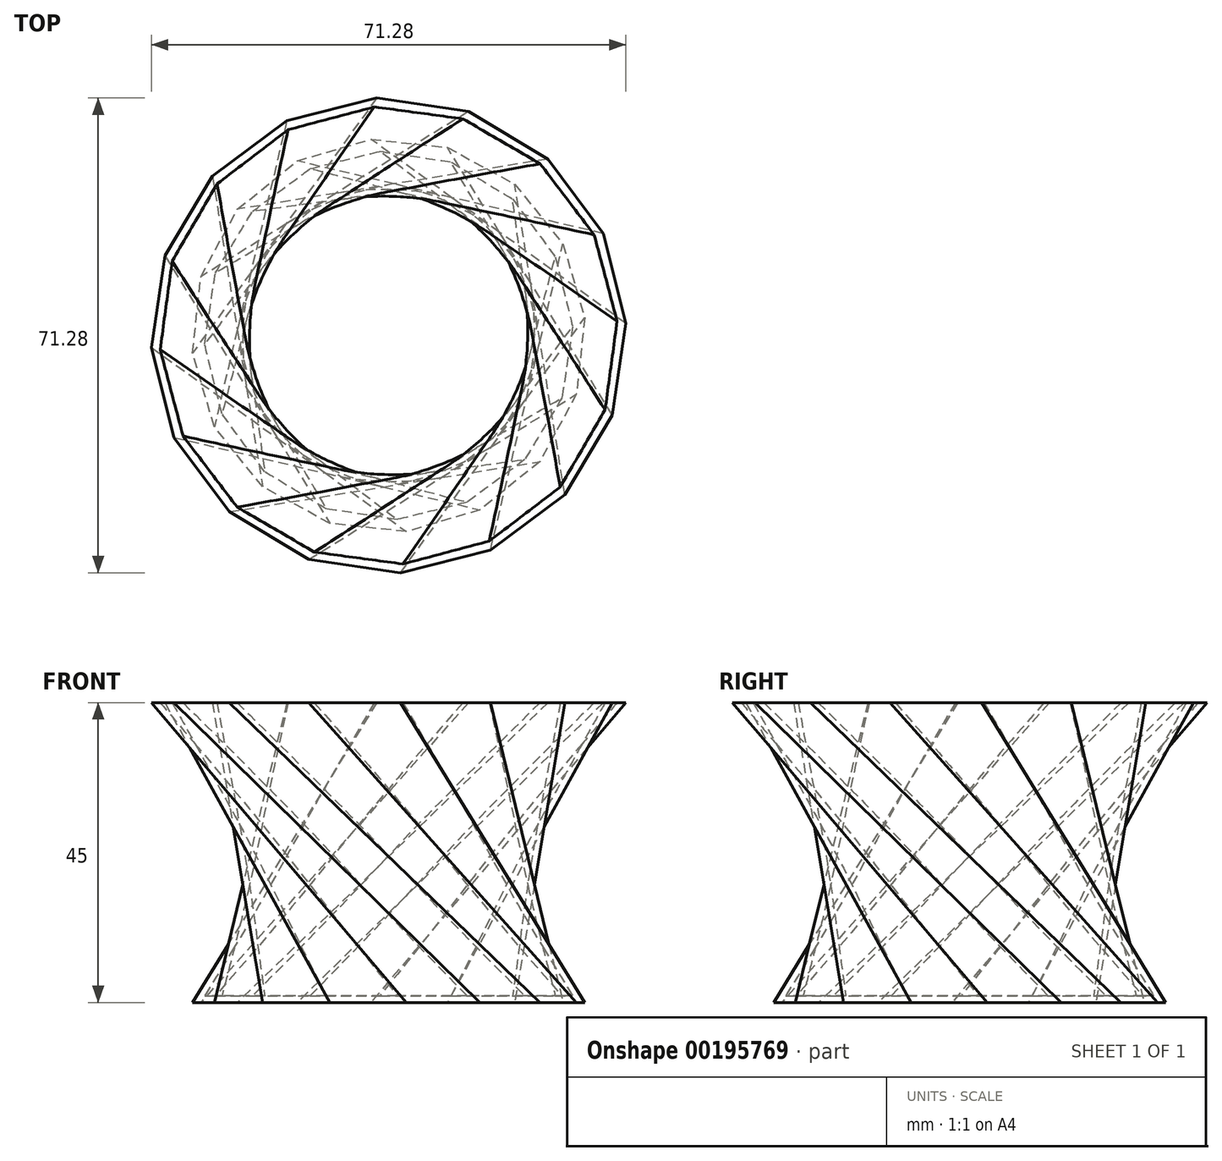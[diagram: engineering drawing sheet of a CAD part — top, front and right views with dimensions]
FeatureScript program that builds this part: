
annotation { "Feature Type Name" : "Feature", "Feature Type Description" : "" }
export const myFeature = defineFeature(function(context is Context, id is Id, definition is map)
    precondition{}
    {
        {
            var Q0;
            Q0=qCreatedBy(makeId("Top.planeOp"),FACE);
            var sketch = newSketch(context, id + "F0", { "sketchPlane" : qUnion([Q0])});
            skCircle(sketch, "E0.cCircle", {"center": v(0, 0) * mm, "radius": 29 * mm, "construction": true});
            skLineSegment(sketch, "E0.0", {"start": v(22.7, -18.94) * mm, "end": v(13.73, -26.19) * mm});
            skLineSegment(sketch, "E0.1", {"start": v(13.73, -26.19) * mm, "end": v(2.66, -29.45) * mm});
            skLineSegment(sketch, "E0.2", {"start": v(2.66, -29.45) * mm, "end": v(-8.81, -28.22) * mm});
            skLineSegment(sketch, "E0.3", {"start": v(-8.81, -28.22) * mm, "end": v(-18.94, -22.7) * mm});
            skLineSegment(sketch, "E0.4", {"start": v(-18.94, -22.7) * mm, "end": v(-26.19, -13.73) * mm});
            skLineSegment(sketch, "E0.5", {"start": v(-26.19, -13.73) * mm, "end": v(-29.45, -2.66) * mm});
            skLineSegment(sketch, "E0.6", {"start": v(-29.45, -2.66) * mm, "end": v(-28.22, 8.81) * mm});
            skLineSegment(sketch, "E0.7", {"start": v(-28.22, 8.81) * mm, "end": v(-22.7, 18.94) * mm});
            skLineSegment(sketch, "E0.8", {"start": v(-22.7, 18.94) * mm, "end": v(-13.73, 26.19) * mm});
            skLineSegment(sketch, "E0.9", {"start": v(-13.73, 26.19) * mm, "end": v(-2.66, 29.45) * mm});
            skLineSegment(sketch, "E0.10", {"start": v(-2.66, 29.45) * mm, "end": v(8.81, 28.22) * mm});
            skLineSegment(sketch, "E0.11", {"start": v(8.81, 28.22) * mm, "end": v(18.94, 22.7) * mm});
            skLineSegment(sketch, "E0.12", {"start": v(18.94, 22.7) * mm, "end": v(26.19, 13.73) * mm});
            skLineSegment(sketch, "E0.13", {"start": v(26.19, 13.73) * mm, "end": v(29.45, 2.66) * mm});
            skLineSegment(sketch, "E0.14", {"start": v(29.45, 2.66) * mm, "end": v(28.22, -8.81) * mm});
            skLineSegment(sketch, "E0.15", {"start": v(28.22, -8.81) * mm, "end": v(22.7, -18.94) * mm});
            skPoint(sketch, "E0.0.midPoint", {"position": v(18.21, -22.57) * mm});
            skSolve(sketch);
        }
        {
            var Q0;
            Q0=qCreatedBy(makeId("Top.planeOp"),FACE);
            cPlane(context, id + "F1", {"entities" : qUnion([Q0]), "cplaneType" : CPlaneType.OFFSET, "offset" : 45 * mm, "width" : 150 * mm, "height" : 150 * mm});
        }
        {
            var Q0;
            Q0=qCreatedBy(id+"F1.planeOp",FACE);
            var sketch = newSketch(context, id + "F2", { "sketchPlane" : qUnion([Q0])});
            skCircle(sketch, "E1.cCircle", {"center": v(0, 0) * mm, "radius": 35 * mm, "construction": true});
            skLineSegment(sketch, "E1.0", {"start": v(-23.93, -26.47) * mm, "end": v(-32.24, -15.3) * mm});
            skLineSegment(sketch, "E1.1", {"start": v(-32.24, -15.3) * mm, "end": v(-35.64, -1.8) * mm});
            skLineSegment(sketch, "E1.2", {"start": v(-35.64, -1.8) * mm, "end": v(-33.61, 11.98) * mm});
            skLineSegment(sketch, "E1.3", {"start": v(-33.61, 11.98) * mm, "end": v(-26.47, 23.93) * mm});
            skLineSegment(sketch, "E1.4", {"start": v(-26.47, 23.93) * mm, "end": v(-15.3, 32.24) * mm});
            skLineSegment(sketch, "E1.5", {"start": v(-15.3, 32.24) * mm, "end": v(-1.8, 35.64) * mm});
            skLineSegment(sketch, "E1.6", {"start": v(-1.8, 35.64) * mm, "end": v(11.98, 33.61) * mm});
            skLineSegment(sketch, "E1.7", {"start": v(11.98, 33.61) * mm, "end": v(23.93, 26.47) * mm});
            skLineSegment(sketch, "E1.8", {"start": v(23.93, 26.47) * mm, "end": v(32.24, 15.3) * mm});
            skLineSegment(sketch, "E1.9", {"start": v(32.24, 15.3) * mm, "end": v(35.64, 1.8) * mm});
            skLineSegment(sketch, "E1.10", {"start": v(35.64, 1.8) * mm, "end": v(33.61, -11.98) * mm});
            skLineSegment(sketch, "E1.11", {"start": v(33.61, -11.98) * mm, "end": v(26.47, -23.93) * mm});
            skLineSegment(sketch, "E1.12", {"start": v(26.47, -23.93) * mm, "end": v(15.3, -32.24) * mm});
            skLineSegment(sketch, "E1.13", {"start": v(15.3, -32.24) * mm, "end": v(1.8, -35.64) * mm});
            skLineSegment(sketch, "E1.14", {"start": v(1.8, -35.64) * mm, "end": v(-11.98, -33.61) * mm});
            skLineSegment(sketch, "E1.15", {"start": v(-11.98, -33.61) * mm, "end": v(-23.93, -26.47) * mm});
            skPoint(sketch, "E1.0.midPoint", {"position": v(-28.09, -20.88) * mm});
            skSolve(sketch);
        }
        {
            var Q0;
            Q0=makeQuery(id+"F2.imprint","IMPRINT",FACE,{"disambiguationData":[TD([[makeQuery(id+"F2.imprint","IMPRINT",EDGE,{"derivedFrom":sQuery(id+"F2.wireOp",EDGE,"E1.0")}),-1.0]])]});
            var Q1;
            Q1=makeQuery(id+"F0.imprint","IMPRINT",FACE,{"disambiguationData":[TD([[makeQuery(id+"F0.imprint","IMPRINT",EDGE,{"derivedFrom":sQuery(id+"F0.wireOp",EDGE,"E0.0")}),-1.0]])]});
            var Q2;
            Q2=sQuery(id+"F0.wireOp",VERTEX,"E0.2.start");
            var Q3;
            Q3=sQuery(id+"F2.wireOp",VERTEX,"E1.2.start");
            loft(context, id + "F3", {"sheetProfilesArray" : [{ "sheetProfileEntities" : qUnion([Q0]) }, { "sheetProfileEntities" : qUnion([Q1]) }], "matchConnections" : true, "connections" : [{ "connectionEntities" : qUnion([Q2, Q3]), "connectionEdgeQueries" : qUnion([]), "connectionEdgeParameters" : [] }]});
        }
        {
            var Q0;
            Q0=makeQuery(id+"F3.opLoft","CAP_FACE",FACE,{"disambiguationData":[OSD([makeQuery(id+"F2.imprint","IMPRINT",FACE,{"disambiguationData":[TD([[makeQuery(id+"F2.imprint","IMPRINT",EDGE,{"derivedFrom":sQuery(id+"F2.wireOp",EDGE,"E1.0")}),-1.0]])]})])],"isStart":true});
            shell(context, id + "F4", {"entities" : qUnion([Q0]), "thickness" : 1 * mm});
        }
    });
